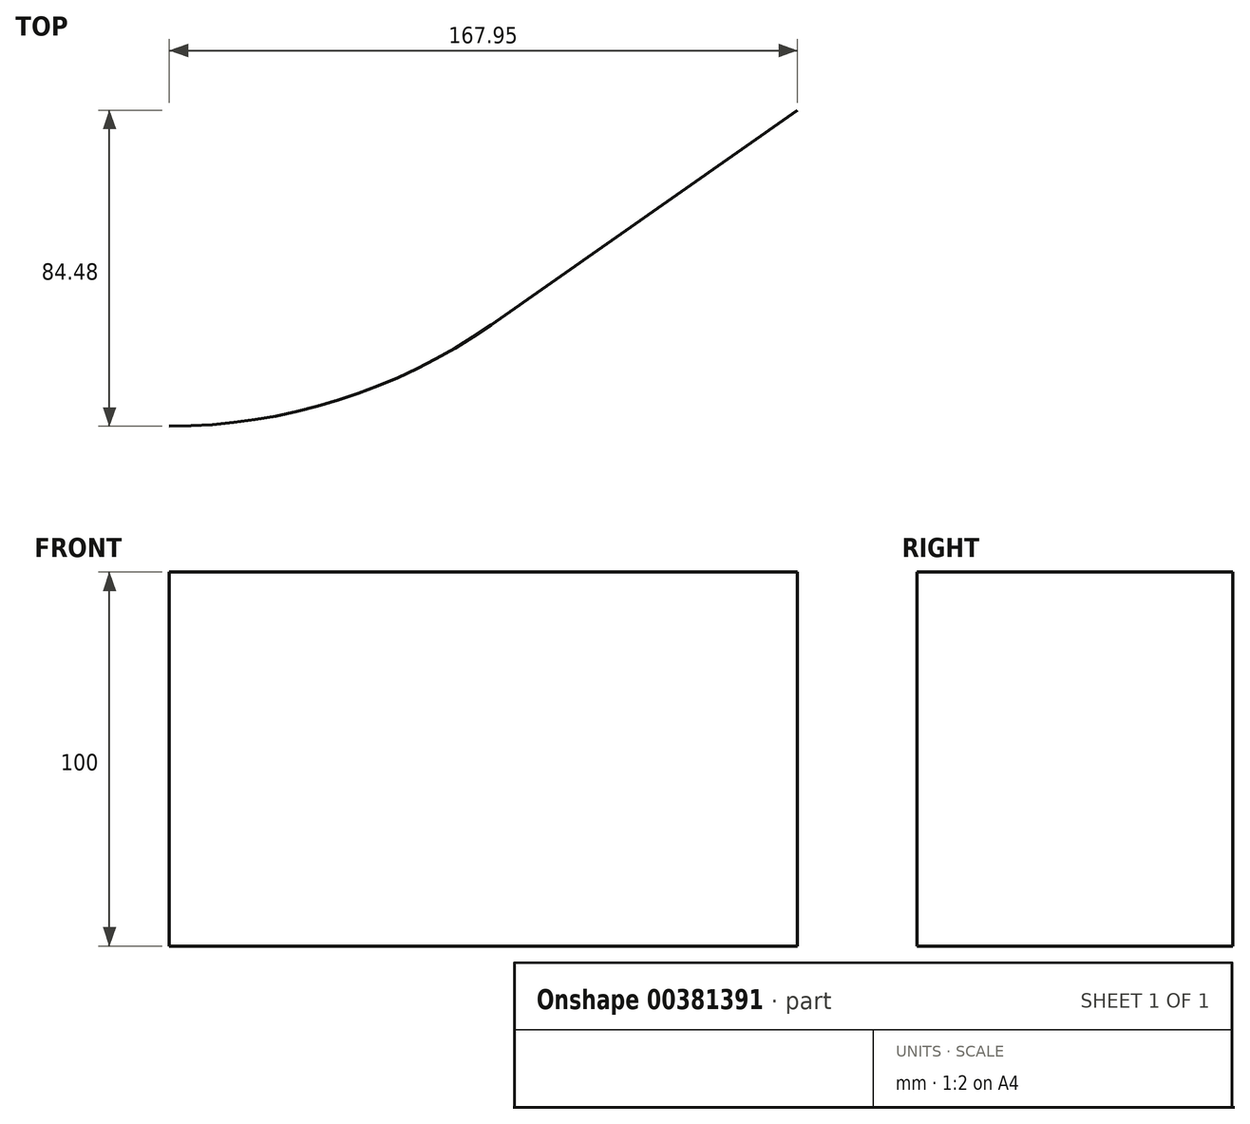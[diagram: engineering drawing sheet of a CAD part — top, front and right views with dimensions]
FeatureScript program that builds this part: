
annotation { "Feature Type Name" : "Feature", "Feature Type Description" : "" }
export const myFeature = defineFeature(function(context is Context, id is Id, definition is map)
    precondition{}
    {
        {
            var Q0;
            Q0=qCreatedBy(makeId("Top.planeOp"),FACE);
            var sketch = newSketch(context, id + "F0", { "sketchPlane" : qUnion([Q0])});
            skArc(sketch, "E0", {"start": v(0, -150) * mm, "mid": v(45.1, -143.06) * mm, "end": v(86.04, -122.87) * mm});
            skLineSegment(sketch, "E1", {"start": v(86.04, -122.87) * mm, "end": v(167.95, -65.52) * mm});
            skLineSegment(sketch, "E2", {"start": v(0, 0) * mm, "end": v(86.04, -122.87) * mm, "construction": true});
            skLineSegment(sketch, "E3", {"start": v(0, 0) * mm, "end": v(0, -150) * mm, "construction": true});
            skSolve(sketch);
        }
        {
            var Q0;
            Q0=sQuery(id+"F0.wireOp",EDGE,"E0");
            var Q1;
            Q1=sQuery(id+"F0.wireOp",EDGE,"E1");
            extrude(context, id + "F1", {"bodyType" : ToolBodyType.SURFACE, "surfaceEntities" : qUnion([Q0, Q1]), "depth" : 100 * mm});
        }
    });
